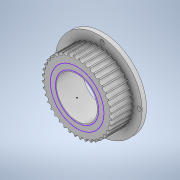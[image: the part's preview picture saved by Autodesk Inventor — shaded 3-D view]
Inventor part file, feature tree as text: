
AUTODESK INVENTOR PART (.ipt)
format: ipt  version: 2021 (Build 250183000, 183)  size: 254,976 bytes
history: native  units: in
note: dims shown in document units (in); Inventor stores cm internally (conversion verified against a paired STEP export)
features: sketch x8, hole x4, extrude x3
ambient origin geometry x8: Origin, YZ Plane, XZ Plane, XY Plane, X Axis, Y Axis, Z Axis, Center Point
bodies: Solid1 (feature_tree)
feature tree (15):
  extrude  "Extrusion1"  Depth=10.0in TaperAngle=0.0deg
  extrude  "Extrusion2"  Depth=10.0in
  extrude  "Extrusion3"  Depth=50.0in TaperAngle=0.0deg
  sketch  "Sketch4"  dims[d11=167.625in d12=0.0in]
  hole  "Hole1"  [1 undecoded]
  hole  "Hole2"  [1 undecoded]
  hole  "Hole3"  [1 undecoded]
  hole  "Hole4"  [1 undecoded]
  sketch  "Sketch1"  dims[d0=200.0in d1=10.0in d2=0.0in]
  sketch  "Sketch2"  dims[d3=160.0in d4=10.0in]
  sketch  "Sketch3"  dims[d5=15.748in d7=360.0deg d9=50.0in d10=0.0in]
  sketch  "Sketch5"  dims[d13=10.0in d14=0.75in d15=0.375in d16=0.25in d17=0.5635in d18=1.0in d19=0.8108in]
  sketch  "Sketch6"  dims[d20=10.0in d21=0.75in d22=0.375in d23=0.25in d24=0.5635in d25=1.0in d26=0.8108in]
  sketch  "Sketch7"  dims[d27=10.0in d28=0.75in d29=0.375in d30=0.25in d31=0.5635in d32=1.0in d33=0.8108in]
  sketch  "Sketch8"  dims[d34=10.0in d35=0.75in d36=0.375in d37=0.25in d38=0.5635in d39=1.0in d40=0.8108in d6=0.0344in d8=0.0344in]
note: 4 required parameter values undecoded (feature->parameter linkage not recoverable at this tier; creation-order binding heuristic only, values carry confidence <= 0.55)
